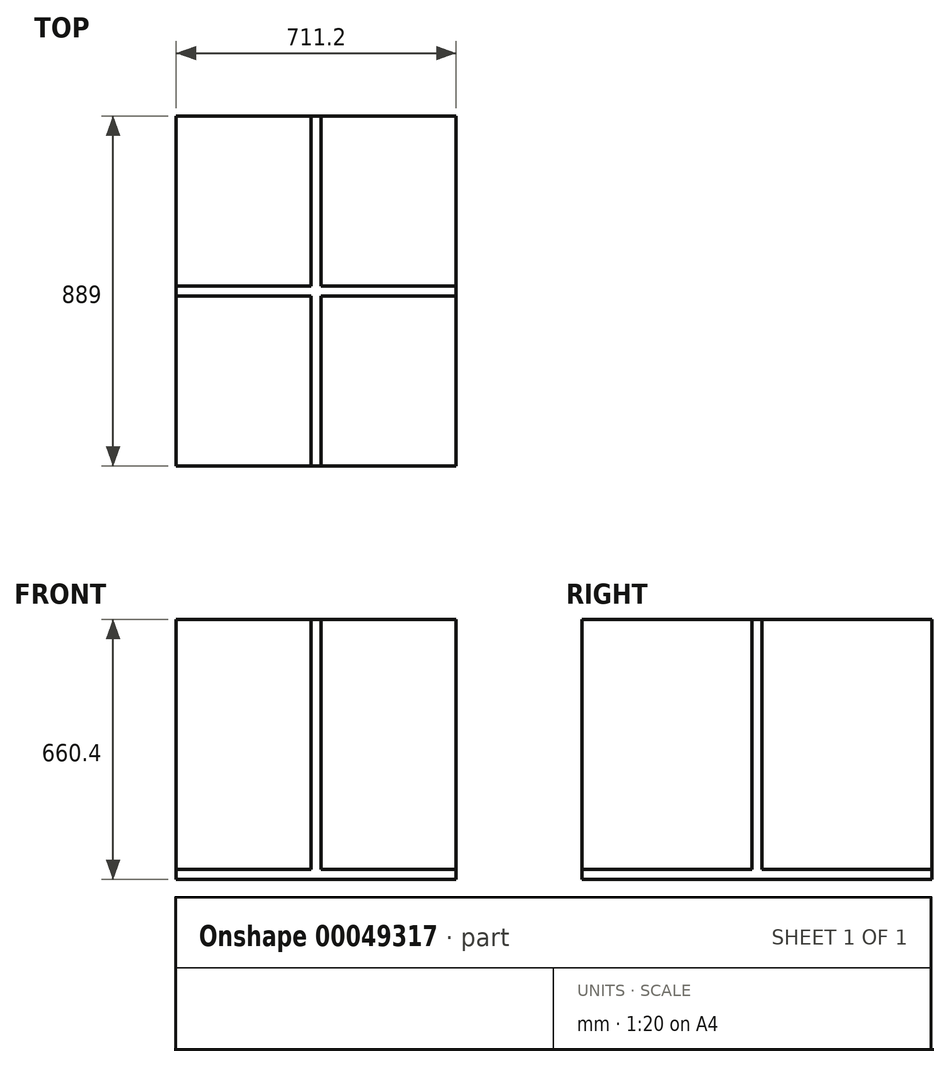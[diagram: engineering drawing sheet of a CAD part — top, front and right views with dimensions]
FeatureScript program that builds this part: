
annotation { "Feature Type Name" : "Feature", "Feature Type Description" : "" }
export const myFeature = defineFeature(function(context is Context, id is Id, definition is map)
    precondition{}
    {
        {
            var Q0;
            Q0=qCreatedBy(makeId("Top.planeOp"),FACE);
            var sketch = newSketch(context, id + "F0", { "sketchPlane" : qUnion([Q0])});
            skLineSegment(sketch, "E0.rect.bottom", {"start": v(-355.6, 444.5) * mm, "end": v(355.6, 444.5) * mm});
            skLineSegment(sketch, "E0.rect.top", {"start": v(-355.6, -444.5) * mm, "end": v(355.6, -444.5) * mm});
            skLineSegment(sketch, "E0.rect.left", {"start": v(-355.6, 444.5) * mm, "end": v(-355.6, -444.5) * mm});
            skLineSegment(sketch, "E0.rect.right", {"start": v(355.6, 444.5) * mm, "end": v(355.6, -444.5) * mm});
            skPoint(sketch, "E0.rect.middle", {"position": v(0, 0) * mm});
            skSolve(sketch);
        }
        {
            var Q0;
            Q0=makeQuery(id+"F0.imprint","IMPRINT",FACE,{"disambiguationData":[TD([[makeQuery(id+"F0.imprint","IMPRINT",EDGE,{"derivedFrom":sQuery(id+"F0.wireOp",EDGE,"E0.rect.bottom")}),-1.0]])]});
            var sketch = newSketch(context, id + "F1", { "sketchPlane" : qUnion([Q0])});
            skLineSegment(sketch, "E1.0", {"start": v(-355.6, -444.5) * mm, "end": v(355.6, -444.5) * mm, "construction": true});
            skLineSegment(sketch, "E1.1", {"start": v(355.6, 444.5) * mm, "end": v(355.6, -444.5) * mm, "construction": true});
            skLineSegment(sketch, "E1.2", {"start": v(-355.6, 444.5) * mm, "end": v(-355.6, -444.5) * mm, "construction": true});
            skLineSegment(sketch, "E1.3", {"start": v(-355.6, 444.5) * mm, "end": v(355.6, 444.5) * mm, "construction": true});
            skLineSegment(sketch, "E2.rect.bottom", {"start": v(-12.7, 444.5) * mm, "end": v(12.7, 444.5) * mm});
            skLineSegment(sketch, "E2.rect.top", {"start": v(-12.7, -444.5) * mm, "end": v(12.7, -444.5) * mm});
            skLineSegment(sketch, "E2.rect.left", {"start": v(-12.7, 444.5) * mm, "end": v(-12.7, 12.7) * mm});
            skLineSegment(sketch, "E2.rect.right", {"start": v(12.7, 444.5) * mm, "end": v(12.7, 12.7) * mm});
            skPoint(sketch, "E2.rect.middle", {"position": v(0, 0) * mm});
            skLineSegment(sketch, "E3.rect.bottom", {"start": v(-355.6, -12.7) * mm, "end": v(-12.7, -12.7) * mm});
            skLineSegment(sketch, "E3.rect.top", {"start": v(-355.6, 12.7) * mm, "end": v(-12.7, 12.7) * mm});
            skLineSegment(sketch, "E3.rect.left", {"start": v(-355.6, -12.7) * mm, "end": v(-355.6, 12.7) * mm});
            skLineSegment(sketch, "E3.rect.right", {"start": v(355.6, -12.7) * mm, "end": v(355.6, 12.7) * mm});
            skLineSegment(sketch, "E4.trimOffspring", {"start": v(12.7, 12.7) * mm, "end": v(355.6, 12.7) * mm});
            skLineSegment(sketch, "E5.trimOffspring", {"start": v(12.7, -12.7) * mm, "end": v(12.7, -444.5) * mm});
            skLineSegment(sketch, "E6.trimOffspring", {"start": v(12.7, -12.7) * mm, "end": v(355.6, -12.7) * mm});
            skLineSegment(sketch, "E7.trimOffspring", {"start": v(-12.7, -12.7) * mm, "end": v(-12.7, -444.5) * mm});
            skSolve(sketch);
        }
        {
            var Q0;
            Q0=makeQuery(id+"F1.imprint","IMPRINT",FACE,{"disambiguationData":[TD([[makeQuery(id+"F1.imprint","IMPRINT",EDGE,{"derivedFrom":sQuery(id+"F1.wireOp",EDGE,"E2.rect.bottom")}),-1.0]])]});
            extrude(context, id + "F2", {"entities" : qUnion([Q0]), "depth" : 635 * mm});
        }
        {
            var Q0;
            Q0=makeQuery(id+"F0.imprint","IMPRINT",FACE,{"disambiguationData":[TD([[makeQuery(id+"F0.imprint","IMPRINT",EDGE,{"derivedFrom":sQuery(id+"F0.wireOp",EDGE,"E0.rect.bottom")}),-1.0]])]});
            extrude(context, id + "F3", {"entities" : qUnion([Q0]), "operationType" : NewBodyOperationType.ADD, "oppositeDirection" : true, "depth" : 25.4 * mm});
        }
    });
